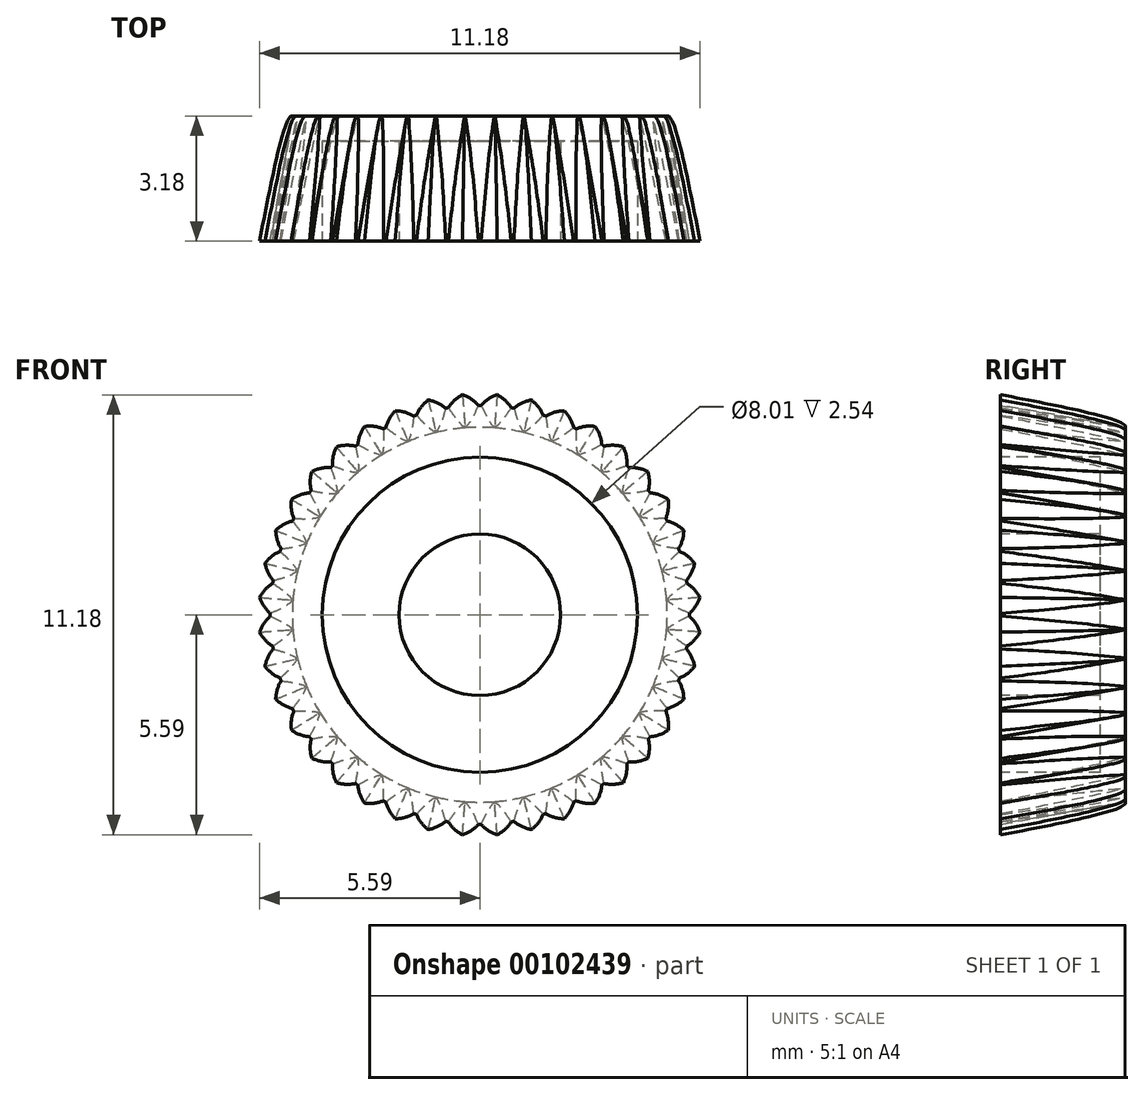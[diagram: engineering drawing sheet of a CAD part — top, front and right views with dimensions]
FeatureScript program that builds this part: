
annotation { "Feature Type Name" : "Feature", "Feature Type Description" : "" }
export const myFeature = defineFeature(function(context is Context, id is Id, definition is map)
    precondition{}
    {
        {
            var Q0;
            Q0=qCreatedBy(makeId("Front.planeOp"),FACE);
            var sketch = newSketch(context, id + "F0", { "sketchPlane" : qUnion([Q0])});
            skCircle(sketch, "E0", {"center": v(0, 0) * mm, "radius": 4.76 * mm});
            skArc(sketch, "E1", {"start": v(0.38, 4.75) * mm, "mid": v(0, 5.14) * mm, "end": v(-0.38, 4.75) * mm});
            skArc(sketch, "E2.1.0", {"start": v(-0.37, 4.75) * mm, "mid": v(-0.8, 5.08) * mm, "end": v(-1.12, 4.63) * mm});
            skArc(sketch, "E2.2.0", {"start": v(-1.1, 4.63) * mm, "mid": v(-1.59, 4.9) * mm, "end": v(-1.83, 4.4) * mm});
            skArc(sketch, "E2.3.0", {"start": v(-1.82, 4.4) * mm, "mid": v(-2.34, 4.58) * mm, "end": v(-2.5, 4.06) * mm});
            skArc(sketch, "E2.4.0", {"start": v(-2.48, 4.06) * mm, "mid": v(-3.02, 4.16) * mm, "end": v(-3.1, 3.62) * mm});
            skArc(sketch, "E2.5.0", {"start": v(-3.09, 3.63) * mm, "mid": v(-3.64, 3.64) * mm, "end": v(-3.63, 3.09) * mm});
            skArc(sketch, "E2.6.0", {"start": v(-3.62, 3.1) * mm, "mid": v(-4.16, 3.02) * mm, "end": v(-4.06, 2.48) * mm});
            skArc(sketch, "E2.7.0", {"start": v(-4.06, 2.5) * mm, "mid": v(-4.58, 2.34) * mm, "end": v(-4.4, 1.82) * mm});
            skArc(sketch, "E2.8.0", {"start": v(-4.4, 1.83) * mm, "mid": v(-4.9, 1.59) * mm, "end": v(-4.63, 1.1) * mm});
            skArc(sketch, "E2.9.0", {"start": v(-4.63, 1.12) * mm, "mid": v(-5.08, 0.8) * mm, "end": v(-4.75, 0.37) * mm});
            skArc(sketch, "E2.10.0", {"start": v(-4.75, 0.38) * mm, "mid": v(-5.14, 0) * mm, "end": v(-4.75, -0.38) * mm});
            skArc(sketch, "E2.11.0", {"start": v(-4.75, -0.37) * mm, "mid": v(-5.08, -0.8) * mm, "end": v(-4.63, -1.12) * mm});
            skArc(sketch, "E2.12.0", {"start": v(-4.63, -1.1) * mm, "mid": v(-4.9, -1.59) * mm, "end": v(-4.4, -1.83) * mm});
            skArc(sketch, "E2.13.0", {"start": v(-4.4, -1.82) * mm, "mid": v(-4.58, -2.34) * mm, "end": v(-4.06, -2.5) * mm});
            skArc(sketch, "E2.14.0", {"start": v(-4.06, -2.48) * mm, "mid": v(-4.16, -3.02) * mm, "end": v(-3.62, -3.1) * mm});
            skArc(sketch, "E2.15.0", {"start": v(-3.63, -3.09) * mm, "mid": v(-3.64, -3.64) * mm, "end": v(-3.09, -3.63) * mm});
            skArc(sketch, "E2.16.0", {"start": v(-3.1, -3.62) * mm, "mid": v(-3.02, -4.16) * mm, "end": v(-2.48, -4.06) * mm});
            skArc(sketch, "E2.17.0", {"start": v(-2.5, -4.06) * mm, "mid": v(-2.34, -4.58) * mm, "end": v(-1.82, -4.4) * mm});
            skArc(sketch, "E2.18.0", {"start": v(-1.83, -4.4) * mm, "mid": v(-1.59, -4.9) * mm, "end": v(-1.1, -4.63) * mm});
            skArc(sketch, "E2.19.0", {"start": v(-1.12, -4.63) * mm, "mid": v(-0.8, -5.08) * mm, "end": v(-0.37, -4.75) * mm});
            skArc(sketch, "E2.20.0", {"start": v(-0.38, -4.75) * mm, "mid": v(0, -5.14) * mm, "end": v(0.38, -4.75) * mm});
            skArc(sketch, "E2.21.0", {"start": v(0.37, -4.75) * mm, "mid": v(0.8, -5.08) * mm, "end": v(1.12, -4.63) * mm});
            skArc(sketch, "E2.22.0", {"start": v(1.1, -4.63) * mm, "mid": v(1.59, -4.9) * mm, "end": v(1.83, -4.4) * mm});
            skArc(sketch, "E2.23.0", {"start": v(1.82, -4.4) * mm, "mid": v(2.34, -4.58) * mm, "end": v(2.5, -4.06) * mm});
            skArc(sketch, "E2.24.0", {"start": v(2.48, -4.06) * mm, "mid": v(3.02, -4.16) * mm, "end": v(3.1, -3.62) * mm});
            skArc(sketch, "E2.25.0", {"start": v(3.09, -3.63) * mm, "mid": v(3.64, -3.64) * mm, "end": v(3.63, -3.09) * mm});
            skArc(sketch, "E2.26.0", {"start": v(3.62, -3.1) * mm, "mid": v(4.16, -3.02) * mm, "end": v(4.06, -2.48) * mm});
            skArc(sketch, "E2.27.0", {"start": v(4.06, -2.5) * mm, "mid": v(4.58, -2.34) * mm, "end": v(4.4, -1.82) * mm});
            skArc(sketch, "E2.28.0", {"start": v(4.4, -1.83) * mm, "mid": v(4.9, -1.59) * mm, "end": v(4.63, -1.1) * mm});
            skArc(sketch, "E2.29.0", {"start": v(4.63, -1.12) * mm, "mid": v(5.08, -0.8) * mm, "end": v(4.75, -0.37) * mm});
            skArc(sketch, "E2.30.0", {"start": v(4.75, -0.38) * mm, "mid": v(5.14, 0) * mm, "end": v(4.75, 0.38) * mm});
            skArc(sketch, "E2.31.0", {"start": v(4.75, 0.37) * mm, "mid": v(5.08, 0.8) * mm, "end": v(4.63, 1.12) * mm});
            skArc(sketch, "E2.32.0", {"start": v(4.63, 1.1) * mm, "mid": v(4.9, 1.59) * mm, "end": v(4.4, 1.83) * mm});
            skArc(sketch, "E2.33.0", {"start": v(4.4, 1.82) * mm, "mid": v(4.58, 2.34) * mm, "end": v(4.06, 2.5) * mm});
            skArc(sketch, "E2.34.0", {"start": v(4.06, 2.48) * mm, "mid": v(4.16, 3.02) * mm, "end": v(3.62, 3.1) * mm});
            skArc(sketch, "E2.35.0", {"start": v(3.63, 3.09) * mm, "mid": v(3.64, 3.64) * mm, "end": v(3.09, 3.63) * mm});
            skArc(sketch, "E2.36.0", {"start": v(3.1, 3.62) * mm, "mid": v(3.02, 4.16) * mm, "end": v(2.48, 4.06) * mm});
            skArc(sketch, "E2.37.0", {"start": v(2.5, 4.06) * mm, "mid": v(2.34, 4.58) * mm, "end": v(1.82, 4.4) * mm});
            skArc(sketch, "E2.38.0", {"start": v(1.83, 4.4) * mm, "mid": v(1.59, 4.9) * mm, "end": v(1.1, 4.63) * mm});
            skArc(sketch, "E2.39.0", {"start": v(1.12, 4.63) * mm, "mid": v(0.8, 5.08) * mm, "end": v(0.37, 4.75) * mm});
            skSolve(sketch);
        }
        {
            var Q0;
            {var subQ0=sQuery(id+"F0.wireOp",EDGE,"E2.2.0");Q0=makeQuery(id+"F0.imprint","IMPRINT",FACE,{"disambiguationData":[TD([[makeQuery(id+"F0.imprint","IMPRINT",EDGE,{"derivedFrom":subQ0}),1.0]])]});}
            var Q1;
            {var subQ0=sQuery(id+"F0.wireOp",EDGE,"E2.1.0");Q1=makeQuery(id+"F0.imprint","IMPRINT",FACE,{"disambiguationData":[TD([[makeQuery(id+"F0.imprint","IMPRINT",EDGE,{"derivedFrom":subQ0}),1.0]])]});}
            var Q2;
            {var subQ0=sQuery(id+"F0.wireOp",EDGE,"E1");Q2=makeQuery(id+"F0.imprint","IMPRINT",FACE,{"disambiguationData":[TD([[makeQuery(id+"F0.imprint","IMPRINT",EDGE,{"derivedFrom":subQ0}),1.0]])]});}
            var Q3;
            {var subQ0=sQuery(id+"F0.wireOp",EDGE,"E2.39.0");Q3=makeQuery(id+"F0.imprint","IMPRINT",FACE,{"disambiguationData":[TD([[makeQuery(id+"F0.imprint","IMPRINT",EDGE,{"derivedFrom":subQ0}),1.0]])]});}
            var Q4;
            {var subQ0=sQuery(id+"F0.wireOp",EDGE,"E2.38.0");Q4=makeQuery(id+"F0.imprint","IMPRINT",FACE,{"disambiguationData":[TD([[makeQuery(id+"F0.imprint","IMPRINT",EDGE,{"derivedFrom":subQ0}),1.0]])]});}
            var Q5;
            {var subQ0=sQuery(id+"F0.wireOp",EDGE,"E2.37.0");Q5=makeQuery(id+"F0.imprint","IMPRINT",FACE,{"disambiguationData":[TD([[makeQuery(id+"F0.imprint","IMPRINT",EDGE,{"derivedFrom":subQ0}),1.0]])]});}
            var Q6;
            {var subQ1=sQuery(id+"F0.wireOp",EDGE,"E0");var subQ53=sQuery(id+"F0.wireOp",EDGE,"E2.30.0");var subQ54=makeQuery(id+"F0.imprint","INTERSECT",VERTEX,{"disambiguationData":[OD(1.0)],"derivedFrom":[subQ1,subQ53]});Q6=makeQuery(id+"F0.imprint","IMPRINT",FACE,{"disambiguationData":[TD([[makeQuery(id+"F0.imprint","IMPRINT",EDGE,{"disambiguationData":[TD([[subQ54,-1.0]])],"derivedFrom":subQ1}),1.0]])]});}
            var Q7;
            {var subQ0=sQuery(id+"F0.wireOp",EDGE,"E2.36.0");Q7=makeQuery(id+"F0.imprint","IMPRINT",FACE,{"disambiguationData":[TD([[makeQuery(id+"F0.imprint","IMPRINT",EDGE,{"derivedFrom":subQ0}),1.0]])]});}
            var Q8;
            {var subQ0=sQuery(id+"F0.wireOp",EDGE,"E2.35.0");Q8=makeQuery(id+"F0.imprint","IMPRINT",FACE,{"disambiguationData":[TD([[makeQuery(id+"F0.imprint","IMPRINT",EDGE,{"derivedFrom":subQ0}),1.0]])]});}
            var Q9;
            {var subQ0=sQuery(id+"F0.wireOp",EDGE,"E2.34.0");Q9=makeQuery(id+"F0.imprint","IMPRINT",FACE,{"disambiguationData":[TD([[makeQuery(id+"F0.imprint","IMPRINT",EDGE,{"derivedFrom":subQ0}),1.0]])]});}
            var Q10;
            {var subQ0=sQuery(id+"F0.wireOp",EDGE,"E2.33.0");Q10=makeQuery(id+"F0.imprint","IMPRINT",FACE,{"disambiguationData":[TD([[makeQuery(id+"F0.imprint","IMPRINT",EDGE,{"derivedFrom":subQ0}),1.0]])]});}
            var Q11;
            {var subQ0=sQuery(id+"F0.wireOp",EDGE,"E2.32.0");Q11=makeQuery(id+"F0.imprint","IMPRINT",FACE,{"disambiguationData":[TD([[makeQuery(id+"F0.imprint","IMPRINT",EDGE,{"derivedFrom":subQ0}),1.0]])]});}
            var Q12;
            {var subQ0=sQuery(id+"F0.wireOp",EDGE,"E2.31.0");Q12=makeQuery(id+"F0.imprint","IMPRINT",FACE,{"disambiguationData":[TD([[makeQuery(id+"F0.imprint","IMPRINT",EDGE,{"derivedFrom":subQ0}),1.0]])]});}
            var Q13;
            {var subQ0=sQuery(id+"F0.wireOp",EDGE,"E2.30.0");Q13=makeQuery(id+"F0.imprint","IMPRINT",FACE,{"disambiguationData":[TD([[makeQuery(id+"F0.imprint","IMPRINT",EDGE,{"derivedFrom":subQ0}),1.0]])]});}
            var Q14;
            {var subQ0=sQuery(id+"F0.wireOp",EDGE,"E2.29.0");Q14=makeQuery(id+"F0.imprint","IMPRINT",FACE,{"disambiguationData":[TD([[makeQuery(id+"F0.imprint","IMPRINT",EDGE,{"derivedFrom":subQ0}),1.0]])]});}
            var Q15;
            {var subQ0=sQuery(id+"F0.wireOp",EDGE,"E2.28.0");Q15=makeQuery(id+"F0.imprint","IMPRINT",FACE,{"disambiguationData":[TD([[makeQuery(id+"F0.imprint","IMPRINT",EDGE,{"derivedFrom":subQ0}),1.0]])]});}
            var Q16;
            {var subQ0=sQuery(id+"F0.wireOp",EDGE,"E2.27.0");Q16=makeQuery(id+"F0.imprint","IMPRINT",FACE,{"disambiguationData":[TD([[makeQuery(id+"F0.imprint","IMPRINT",EDGE,{"derivedFrom":subQ0}),1.0]])]});}
            var Q17;
            {var subQ0=sQuery(id+"F0.wireOp",EDGE,"E2.26.0");Q17=makeQuery(id+"F0.imprint","IMPRINT",FACE,{"disambiguationData":[TD([[makeQuery(id+"F0.imprint","IMPRINT",EDGE,{"derivedFrom":subQ0}),1.0]])]});}
            var Q18;
            {var subQ0=sQuery(id+"F0.wireOp",EDGE,"E2.25.0");Q18=makeQuery(id+"F0.imprint","IMPRINT",FACE,{"disambiguationData":[TD([[makeQuery(id+"F0.imprint","IMPRINT",EDGE,{"derivedFrom":subQ0}),1.0]])]});}
            var Q19;
            {var subQ0=sQuery(id+"F0.wireOp",EDGE,"E2.24.0");Q19=makeQuery(id+"F0.imprint","IMPRINT",FACE,{"disambiguationData":[TD([[makeQuery(id+"F0.imprint","IMPRINT",EDGE,{"derivedFrom":subQ0}),1.0]])]});}
            var Q20;
            {var subQ0=sQuery(id+"F0.wireOp",EDGE,"E2.23.0");Q20=makeQuery(id+"F0.imprint","IMPRINT",FACE,{"disambiguationData":[TD([[makeQuery(id+"F0.imprint","IMPRINT",EDGE,{"derivedFrom":subQ0}),1.0]])]});}
            var Q21;
            {var subQ0=sQuery(id+"F0.wireOp",EDGE,"E2.22.0");Q21=makeQuery(id+"F0.imprint","IMPRINT",FACE,{"disambiguationData":[TD([[makeQuery(id+"F0.imprint","IMPRINT",EDGE,{"derivedFrom":subQ0}),1.0]])]});}
            var Q22;
            {var subQ0=sQuery(id+"F0.wireOp",EDGE,"E2.21.0");Q22=makeQuery(id+"F0.imprint","IMPRINT",FACE,{"disambiguationData":[TD([[makeQuery(id+"F0.imprint","IMPRINT",EDGE,{"derivedFrom":subQ0}),1.0]])]});}
            var Q23;
            {var subQ0=sQuery(id+"F0.wireOp",EDGE,"E2.20.0");Q23=makeQuery(id+"F0.imprint","IMPRINT",FACE,{"disambiguationData":[TD([[makeQuery(id+"F0.imprint","IMPRINT",EDGE,{"derivedFrom":subQ0}),1.0]])]});}
            var Q24;
            {var subQ0=sQuery(id+"F0.wireOp",EDGE,"E2.19.0");Q24=makeQuery(id+"F0.imprint","IMPRINT",FACE,{"disambiguationData":[TD([[makeQuery(id+"F0.imprint","IMPRINT",EDGE,{"derivedFrom":subQ0}),1.0]])]});}
            var Q25;
            {var subQ0=sQuery(id+"F0.wireOp",EDGE,"E2.18.0");Q25=makeQuery(id+"F0.imprint","IMPRINT",FACE,{"disambiguationData":[TD([[makeQuery(id+"F0.imprint","IMPRINT",EDGE,{"derivedFrom":subQ0}),1.0]])]});}
            var Q26;
            {var subQ0=sQuery(id+"F0.wireOp",EDGE,"E2.17.0");Q26=makeQuery(id+"F0.imprint","IMPRINT",FACE,{"disambiguationData":[TD([[makeQuery(id+"F0.imprint","IMPRINT",EDGE,{"derivedFrom":subQ0}),1.0]])]});}
            var Q27;
            {var subQ0=sQuery(id+"F0.wireOp",EDGE,"E2.16.0");Q27=makeQuery(id+"F0.imprint","IMPRINT",FACE,{"disambiguationData":[TD([[makeQuery(id+"F0.imprint","IMPRINT",EDGE,{"derivedFrom":subQ0}),1.0]])]});}
            var Q28;
            {var subQ0=sQuery(id+"F0.wireOp",EDGE,"E2.15.0");Q28=makeQuery(id+"F0.imprint","IMPRINT",FACE,{"disambiguationData":[TD([[makeQuery(id+"F0.imprint","IMPRINT",EDGE,{"derivedFrom":subQ0}),1.0]])]});}
            var Q29;
            {var subQ0=sQuery(id+"F0.wireOp",EDGE,"E2.14.0");Q29=makeQuery(id+"F0.imprint","IMPRINT",FACE,{"disambiguationData":[TD([[makeQuery(id+"F0.imprint","IMPRINT",EDGE,{"derivedFrom":subQ0}),1.0]])]});}
            var Q30;
            {var subQ0=sQuery(id+"F0.wireOp",EDGE,"E2.13.0");Q30=makeQuery(id+"F0.imprint","IMPRINT",FACE,{"disambiguationData":[TD([[makeQuery(id+"F0.imprint","IMPRINT",EDGE,{"derivedFrom":subQ0}),1.0]])]});}
            var Q31;
            {var subQ0=sQuery(id+"F0.wireOp",EDGE,"E2.12.0");Q31=makeQuery(id+"F0.imprint","IMPRINT",FACE,{"disambiguationData":[TD([[makeQuery(id+"F0.imprint","IMPRINT",EDGE,{"derivedFrom":subQ0}),1.0]])]});}
            var Q32;
            {var subQ0=sQuery(id+"F0.wireOp",EDGE,"E2.11.0");Q32=makeQuery(id+"F0.imprint","IMPRINT",FACE,{"disambiguationData":[TD([[makeQuery(id+"F0.imprint","IMPRINT",EDGE,{"derivedFrom":subQ0}),1.0]])]});}
            var Q33;
            {var subQ0=sQuery(id+"F0.wireOp",EDGE,"E2.10.0");Q33=makeQuery(id+"F0.imprint","IMPRINT",FACE,{"disambiguationData":[TD([[makeQuery(id+"F0.imprint","IMPRINT",EDGE,{"derivedFrom":subQ0}),1.0]])]});}
            var Q34;
            {var subQ0=sQuery(id+"F0.wireOp",EDGE,"E2.9.0");Q34=makeQuery(id+"F0.imprint","IMPRINT",FACE,{"disambiguationData":[TD([[makeQuery(id+"F0.imprint","IMPRINT",EDGE,{"derivedFrom":subQ0}),1.0]])]});}
            var Q35;
            {var subQ0=sQuery(id+"F0.wireOp",EDGE,"E2.8.0");Q35=makeQuery(id+"F0.imprint","IMPRINT",FACE,{"disambiguationData":[TD([[makeQuery(id+"F0.imprint","IMPRINT",EDGE,{"derivedFrom":subQ0}),1.0]])]});}
            var Q36;
            {var subQ0=sQuery(id+"F0.wireOp",EDGE,"E2.7.0");Q36=makeQuery(id+"F0.imprint","IMPRINT",FACE,{"disambiguationData":[TD([[makeQuery(id+"F0.imprint","IMPRINT",EDGE,{"derivedFrom":subQ0}),1.0]])]});}
            var Q37;
            {var subQ0=sQuery(id+"F0.wireOp",EDGE,"E2.6.0");Q37=makeQuery(id+"F0.imprint","IMPRINT",FACE,{"disambiguationData":[TD([[makeQuery(id+"F0.imprint","IMPRINT",EDGE,{"derivedFrom":subQ0}),1.0]])]});}
            var Q38;
            {var subQ0=sQuery(id+"F0.wireOp",EDGE,"E2.5.0");Q38=makeQuery(id+"F0.imprint","IMPRINT",FACE,{"disambiguationData":[TD([[makeQuery(id+"F0.imprint","IMPRINT",EDGE,{"derivedFrom":subQ0}),1.0]])]});}
            var Q39;
            {var subQ0=sQuery(id+"F0.wireOp",EDGE,"E2.4.0");Q39=makeQuery(id+"F0.imprint","IMPRINT",FACE,{"disambiguationData":[TD([[makeQuery(id+"F0.imprint","IMPRINT",EDGE,{"derivedFrom":subQ0}),1.0]])]});}
            var Q40;
            {var subQ0=sQuery(id+"F0.wireOp",EDGE,"E2.3.0");Q40=makeQuery(id+"F0.imprint","IMPRINT",FACE,{"disambiguationData":[TD([[makeQuery(id+"F0.imprint","IMPRINT",EDGE,{"derivedFrom":subQ0}),1.0]])]});}
            extrude(context, id + "F1", {"entities" : qUnion([Q0, Q1, Q2, Q3, Q4, Q5, Q6, Q7, Q8, Q9, Q10, Q11, Q12, Q13, Q14, Q15, Q16, Q17, Q18, Q19, Q20, Q21, Q22, Q23, Q24, Q25, Q26, Q27, Q28, Q29, Q30, Q31, Q32, Q33, Q34, Q35, Q36, Q37, Q38, Q39, Q40]), "depth" : 3.17 * mm, "hasDraft" : true, "draftAngle" : 10 * degree});
        }
        {
            var Q0;
            Q0=makeQuery(id+"F1.opExtrude","CAP_FACE",FACE,{"disambiguationData":[OSD([sQuery(id+"F0.wireOp",EDGE,"E0"),sQuery(id+"F0.wireOp",EDGE,"E1"),sQuery(id+"F0.wireOp",EDGE,"E2.1.0"),sQuery(id+"F0.wireOp",EDGE,"E2.2.0"),sQuery(id+"F0.wireOp",EDGE,"E2.3.0"),sQuery(id+"F0.wireOp",EDGE,"E2.4.0"),sQuery(id+"F0.wireOp",EDGE,"E2.5.0"),sQuery(id+"F0.wireOp",EDGE,"E2.6.0"),sQuery(id+"F0.wireOp",EDGE,"E2.7.0"),sQuery(id+"F0.wireOp",EDGE,"E2.8.0"),sQuery(id+"F0.wireOp",EDGE,"E2.9.0"),sQuery(id+"F0.wireOp",EDGE,"E2.10.0"),sQuery(id+"F0.wireOp",EDGE,"E2.11.0"),sQuery(id+"F0.wireOp",EDGE,"E2.12.0"),sQuery(id+"F0.wireOp",EDGE,"E2.13.0"),sQuery(id+"F0.wireOp",EDGE,"E2.14.0"),sQuery(id+"F0.wireOp",EDGE,"E2.15.0"),sQuery(id+"F0.wireOp",EDGE,"E2.16.0"),sQuery(id+"F0.wireOp",EDGE,"E2.17.0"),sQuery(id+"F0.wireOp",EDGE,"E2.18.0"),sQuery(id+"F0.wireOp",EDGE,"E2.19.0"),sQuery(id+"F0.wireOp",EDGE,"E2.20.0"),sQuery(id+"F0.wireOp",EDGE,"E2.21.0"),sQuery(id+"F0.wireOp",EDGE,"E2.22.0"),sQuery(id+"F0.wireOp",EDGE,"E2.23.0"),sQuery(id+"F0.wireOp",EDGE,"E2.24.0"),sQuery(id+"F0.wireOp",EDGE,"E2.25.0"),sQuery(id+"F0.wireOp",EDGE,"E2.26.0"),sQuery(id+"F0.wireOp",EDGE,"E2.27.0"),sQuery(id+"F0.wireOp",EDGE,"E2.28.0"),sQuery(id+"F0.wireOp",EDGE,"E2.29.0"),sQuery(id+"F0.wireOp",EDGE,"E2.30.0"),sQuery(id+"F0.wireOp",EDGE,"E2.31.0"),sQuery(id+"F0.wireOp",EDGE,"E2.32.0"),sQuery(id+"F0.wireOp",EDGE,"E2.33.0"),sQuery(id+"F0.wireOp",EDGE,"E2.34.0"),sQuery(id+"F0.wireOp",EDGE,"E2.35.0"),sQuery(id+"F0.wireOp",EDGE,"E2.36.0"),sQuery(id+"F0.wireOp",EDGE,"E2.37.0"),sQuery(id+"F0.wireOp",EDGE,"E2.38.0"),sQuery(id+"F0.wireOp",EDGE,"E2.39.0")])],"isStart":false});
            var sketch = newSketch(context, id + "F2", { "sketchPlane" : qUnion([Q0])});
            skCircle(sketch, "E3", {"center": v(0, 0) * mm, "radius": 4 * mm});
            skCircle(sketch, "E4", {"center": v(0, 0) * mm, "radius": 2.05 * mm});
            skSolve(sketch);
        }
        {
            var Q0;
            Q0=makeQuery(id+"F2.imprint","IMPRINT",FACE,{"disambiguationData":[TD([[makeQuery(id+"F2.imprint","IMPRINT",EDGE,{"derivedFrom":sQuery(id+"F2.wireOp",EDGE,"E3")}),1.0]])]});
            extrude(context, id + "F3", {"entities" : qUnion([Q0]), "operationType" : NewBodyOperationType.REMOVE, "oppositeDirection" : true, "depth" : 2.54 * mm});
        }
    });
